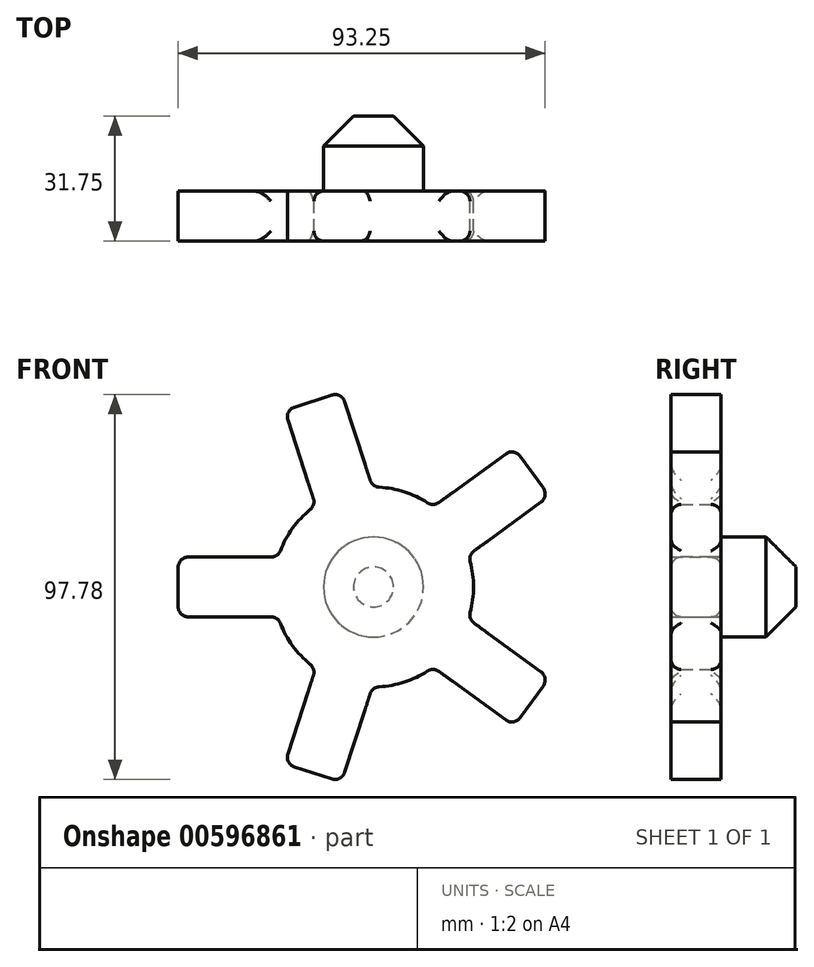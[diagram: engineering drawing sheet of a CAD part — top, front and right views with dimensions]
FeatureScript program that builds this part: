
annotation { "Feature Type Name" : "Feature", "Feature Type Description" : "" }
export const myFeature = defineFeature(function(context is Context, id is Id, definition is map)
    precondition{}
    {
        {
            var Q0;
            Q0=qCreatedBy(makeId("Front.planeOp"),FACE);
            var sketch = newSketch(context, id + "F0", { "sketchPlane" : qUnion([Q0])});
            skCircle(sketch, "E0", {"center": v(0, 0) * mm, "radius": 25.4 * mm});
            skLineSegment(sketch, "E1", {"start": v(-25.4, 0) * mm, "end": v(0, 0) * mm});
            skLineSegment(sketch, "E2.bottom", {"start": v(24.24, 7.59) * mm, "end": v(-49.64, 7.59) * mm});
            skLineSegment(sketch, "E2.top", {"start": v(24.24, -7.59) * mm, "end": v(-49.64, -7.59) * mm});
            skLineSegment(sketch, "E2.left", {"start": v(24.24, 7.59) * mm, "end": v(24.24, -7.59) * mm});
            skLineSegment(sketch, "E2.right", {"start": v(-49.64, 7.59) * mm, "end": v(-49.64, -7.59) * mm});
            skPoint(sketch, "E2.middle", {"position": v(-12.7, 0) * mm});
            skLineSegment(sketch, "E3.1.0", {"start": v(-22.56, -44.87) * mm, "end": v(-8.12, -49.56) * mm});
            skLineSegment(sketch, "E3.1.1", {"start": v(0.28, 25.4) * mm, "end": v(-22.56, -44.87) * mm});
            skLineSegment(sketch, "E3.1.2", {"start": v(14.7, 20.7) * mm, "end": v(-8.12, -49.56) * mm});
            skLineSegment(sketch, "E3.1.3", {"start": v(0.28, 25.4) * mm, "end": v(14.7, 20.7) * mm});
            skLineSegment(sketch, "E3.2.0", {"start": v(35.7, -35.32) * mm, "end": v(44.62, -23.04) * mm});
            skLineSegment(sketch, "E3.2.1", {"start": v(-24.07, 8.11) * mm, "end": v(35.7, -35.32) * mm});
            skLineSegment(sketch, "E3.2.2", {"start": v(-15.15, 20.39) * mm, "end": v(44.62, -23.04) * mm});
            skLineSegment(sketch, "E3.2.3", {"start": v(-24.07, 8.11) * mm, "end": v(-15.15, 20.39) * mm});
            skLineSegment(sketch, "E3.3.0", {"start": v(44.62, 23.04) * mm, "end": v(35.7, 35.32) * mm});
            skLineSegment(sketch, "E3.3.1", {"start": v(-15.15, -20.39) * mm, "end": v(44.62, 23.04) * mm});
            skLineSegment(sketch, "E3.3.2", {"start": v(-24.07, -8.11) * mm, "end": v(35.7, 35.32) * mm});
            skLineSegment(sketch, "E3.3.3", {"start": v(-15.15, -20.39) * mm, "end": v(-24.07, -8.11) * mm});
            skLineSegment(sketch, "E3.4.0", {"start": v(-8.12, 49.56) * mm, "end": v(-22.56, 44.87) * mm});
            skLineSegment(sketch, "E3.4.1", {"start": v(14.7, -20.7) * mm, "end": v(-8.12, 49.56) * mm});
            skLineSegment(sketch, "E3.4.2", {"start": v(0.28, -25.4) * mm, "end": v(-22.56, 44.87) * mm});
            skLineSegment(sketch, "E3.4.3", {"start": v(14.7, -20.7) * mm, "end": v(0.28, -25.4) * mm});
            skSolve(sketch);
        }
        {
            var Q0;
            Q0 = qSketchRegion(id + "F0", true);
            var Q1;
            {var subQ5=sQuery(id+"F0.wireOp",EDGE,"E3.2.2");var subQ6=sQuery(id+"F0.wireOp",EDGE,"E2.bottom");var subQ7=makeQuery(id+"F0.imprint","INTERSECT",VERTEX,{"derivedFrom":[subQ6,subQ5]});Q1=makeQuery(id+"F0.imprint","IMPRINT",FACE,{"disambiguationData":[TD([[makeQuery(id+"F0.imprint","IMPRINT",EDGE,{"disambiguationData":[TD([[subQ7,-1.0]])],"derivedFrom":subQ6}),1.0]])]});}
            var Q2;
            {var subQ0=sQuery(id+"F0.wireOp",EDGE,"E3.4.1");var subQ1=sQuery(id+"F0.wireOp",EDGE,"E3.1.1");var subQ2=makeQuery(id+"F0.imprint","INTERSECT",VERTEX,{"derivedFrom":[subQ1,subQ0]});Q2=makeQuery(id+"F0.imprint","IMPRINT",FACE,{"disambiguationData":[TD([[makeQuery(id+"F0.imprint","IMPRINT",EDGE,{"disambiguationData":[TD([[subQ2,-1.0]])],"derivedFrom":subQ1}),1.0]])]});}
            var Q3;
            {var subQ0=sQuery(id+"F0.wireOp",EDGE,"E3.1.2");var subQ1=sQuery(id+"F0.wireOp",EDGE,"E2.bottom");var subQ2=makeQuery(id+"F0.imprint","INTERSECT",VERTEX,{"derivedFrom":[subQ1,subQ0]});Q3=makeQuery(id+"F0.imprint","IMPRINT",FACE,{"disambiguationData":[TD([[makeQuery(id+"F0.imprint","IMPRINT",EDGE,{"disambiguationData":[TD([[subQ2,-1.0]])],"derivedFrom":subQ1}),-1.0]])]});}
            var Q4;
            {var subQ0=sQuery(id+"F0.wireOp",EDGE,"E3.3.1");var subQ1=sQuery(id+"F0.wireOp",EDGE,"E2.bottom");var subQ2=makeQuery(id+"F0.imprint","INTERSECT",VERTEX,{"derivedFrom":[subQ1,subQ0]});Q4=makeQuery(id+"F0.imprint","IMPRINT",FACE,{"disambiguationData":[TD([[makeQuery(id+"F0.imprint","IMPRINT",EDGE,{"disambiguationData":[TD([[subQ2,-1.0]])],"derivedFrom":subQ1}),1.0]])]});}
            var Q5;
            {var subQ0=sQuery(id+"F0.wireOp",EDGE,"E3.2.2");var subQ1=sQuery(id+"F0.wireOp",EDGE,"E2.top");var subQ2=makeQuery(id+"F0.imprint","INTERSECT",VERTEX,{"derivedFrom":[subQ1,subQ0]});Q5=makeQuery(id+"F0.imprint","IMPRINT",FACE,{"disambiguationData":[TD([[makeQuery(id+"F0.imprint","IMPRINT",EDGE,{"disambiguationData":[TD([[subQ2,-1.0]])],"derivedFrom":subQ1}),-1.0]])]});}
            var Q6;
            {var subQ0=sQuery(id+"F0.wireOp",EDGE,"E3.4.2");var subQ1=sQuery(id+"F0.wireOp",EDGE,"E2.top");var subQ2=makeQuery(id+"F0.imprint","INTERSECT",VERTEX,{"derivedFrom":[subQ1,subQ0]});Q6=makeQuery(id+"F0.imprint","IMPRINT",FACE,{"disambiguationData":[TD([[makeQuery(id+"F0.imprint","IMPRINT",EDGE,{"disambiguationData":[TD([[subQ2,-1.0]])],"derivedFrom":subQ1}),1.0]])]});}
            var Q7;
            {var subQ0=sQuery(id+"F0.wireOp",EDGE,"E3.4.1");var subQ1=sQuery(id+"F0.wireOp",EDGE,"E2.top");var subQ2=makeQuery(id+"F0.imprint","INTERSECT",VERTEX,{"derivedFrom":[subQ1,subQ0]});Q7=makeQuery(id+"F0.imprint","IMPRINT",FACE,{"disambiguationData":[TD([[makeQuery(id+"F0.imprint","IMPRINT",EDGE,{"disambiguationData":[TD([[subQ2,-1.0]])],"derivedFrom":subQ1}),1.0]])]});}
            var Q8;
            {var subQ0=sQuery(id+"F0.wireOp",EDGE,"E3.1.2");var subQ1=sQuery(id+"F0.wireOp",EDGE,"E2.top");var subQ2=makeQuery(id+"F0.imprint","INTERSECT",VERTEX,{"derivedFrom":[subQ1,subQ0]});Q8=makeQuery(id+"F0.imprint","IMPRINT",FACE,{"disambiguationData":[TD([[makeQuery(id+"F0.imprint","IMPRINT",EDGE,{"disambiguationData":[TD([[subQ2,-1.0]])],"derivedFrom":subQ1}),1.0]])]});}
            var Q9;
            {var subQ0=sQuery(id+"F0.wireOp",EDGE,"E3.2.1");var subQ1=sQuery(id+"F0.wireOp",EDGE,"E2.top");var subQ2=makeQuery(id+"F0.imprint","INTERSECT",VERTEX,{"derivedFrom":[subQ1,subQ0]});Q9=makeQuery(id+"F0.imprint","IMPRINT",FACE,{"disambiguationData":[TD([[makeQuery(id+"F0.imprint","IMPRINT",EDGE,{"disambiguationData":[TD([[subQ2,-1.0]])],"derivedFrom":subQ1}),1.0]])]});}
            var Q10;
            {var subQ0=sQuery(id+"F0.wireOp",EDGE,"E3.1.1");var subQ3=sQuery(id+"F0.wireOp",EDGE,"E3.2.1");var subQ5=makeQuery(id+"F0.imprint","INTERSECT",VERTEX,{"derivedFrom":[subQ0,subQ3]});Q10=makeQuery(id+"F0.imprint","IMPRINT",FACE,{"disambiguationData":[TD([[makeQuery(id+"F0.imprint","IMPRINT",EDGE,{"disambiguationData":[TD([[subQ5,1.0]])],"derivedFrom":subQ0}),-1.0]])]});}
            var Q11;
            {var subQ0=sQuery(id+"F0.wireOp",EDGE,"E3.4.2");var subQ1=sQuery(id+"F0.wireOp",EDGE,"E2.bottom");var subQ2=makeQuery(id+"F0.imprint","INTERSECT",VERTEX,{"derivedFrom":[subQ1,subQ0]});Q11=makeQuery(id+"F0.imprint","IMPRINT",FACE,{"disambiguationData":[TD([[makeQuery(id+"F0.imprint","IMPRINT",EDGE,{"disambiguationData":[TD([[subQ2,-1.0]])],"derivedFrom":subQ1}),1.0]])]});}
            var Q12;
            {var subQ0=sQuery(id+"F0.wireOp",EDGE,"E3.1.1");var subQ1=sQuery(id+"F0.wireOp",EDGE,"E2.bottom");var subQ2=makeQuery(id+"F0.imprint","INTERSECT",VERTEX,{"derivedFrom":[subQ1,subQ0]});Q12=makeQuery(id+"F0.imprint","IMPRINT",FACE,{"disambiguationData":[TD([[makeQuery(id+"F0.imprint","IMPRINT",EDGE,{"disambiguationData":[TD([[subQ2,-1.0]])],"derivedFrom":subQ1}),-1.0]])]});}
            var Q13;
            {var subQ0=sQuery(id+"F0.wireOp",EDGE,"E3.2.1");var subQ1=sQuery(id+"F0.wireOp",EDGE,"E3.1.2");var subQ2=makeQuery(id+"F0.imprint","INTERSECT",VERTEX,{"derivedFrom":[subQ1,subQ0]});Q13=makeQuery(id+"F0.imprint","IMPRINT",FACE,{"disambiguationData":[TD([[makeQuery(id+"F0.imprint","IMPRINT",EDGE,{"disambiguationData":[TD([[subQ2,-1.0]])],"derivedFrom":subQ1}),-1.0]])]});}
            var Q14;
            {var subQ0=sQuery(id+"F0.wireOp",EDGE,"E3.1.1");var subQ1=sQuery(id+"F0.wireOp",EDGE,"E2.top");var subQ2=makeQuery(id+"F0.imprint","INTERSECT",VERTEX,{"derivedFrom":[subQ1,subQ0]});Q14=makeQuery(id+"F0.imprint","IMPRINT",FACE,{"disambiguationData":[TD([[makeQuery(id+"F0.imprint","IMPRINT",EDGE,{"disambiguationData":[TD([[subQ2,-1.0]])],"derivedFrom":subQ1}),-1.0]])]});}
            var Q15;
            {var subQ0=sQuery(id+"F0.wireOp",EDGE,"E3.4.2");var subQ1=sQuery(id+"F0.wireOp",EDGE,"E2.top");var subQ2=makeQuery(id+"F0.imprint","INTERSECT",VERTEX,{"derivedFrom":[subQ1,subQ0]});Q15=makeQuery(id+"F0.imprint","IMPRINT",FACE,{"disambiguationData":[TD([[makeQuery(id+"F0.imprint","IMPRINT",EDGE,{"disambiguationData":[TD([[subQ2,-1.0]])],"derivedFrom":subQ1}),-1.0]])]});}
            var Q16;
            {var subQ0=sQuery(id+"F0.wireOp",EDGE,"E3.2.1");var subQ1=sQuery(id+"F0.wireOp",EDGE,"E3.1.1");var subQ2=makeQuery(id+"F0.imprint","INTERSECT",VERTEX,{"derivedFrom":[subQ1,subQ0]});Q16=makeQuery(id+"F0.imprint","IMPRINT",FACE,{"disambiguationData":[TD([[makeQuery(id+"F0.imprint","IMPRINT",EDGE,{"disambiguationData":[TD([[subQ2,-1.0]])],"derivedFrom":subQ0}),1.0]])]});}
            var Q17;
            {var subQ0=sQuery(id+"F0.wireOp",EDGE,"E3.4.2");var subQ3=sQuery(id+"F0.wireOp",EDGE,"E3.3.2");var subQ5=makeQuery(id+"F0.imprint","INTERSECT",VERTEX,{"derivedFrom":[subQ3,subQ0]});Q17=makeQuery(id+"F0.imprint","IMPRINT",FACE,{"disambiguationData":[TD([[makeQuery(id+"F0.imprint","IMPRINT",EDGE,{"disambiguationData":[TD([[subQ5,1.0]])],"derivedFrom":subQ3}),-1.0]])]});}
            var Q18;
            {var subQ0=sQuery(id+"F0.wireOp",EDGE,"E3.1.1");var subQ1=sQuery(id+"F0.wireOp",EDGE,"E2.bottom");var subQ2=makeQuery(id+"F0.imprint","INTERSECT",VERTEX,{"derivedFrom":[subQ1,subQ0]});Q18=makeQuery(id+"F0.imprint","IMPRINT",FACE,{"disambiguationData":[TD([[makeQuery(id+"F0.imprint","IMPRINT",EDGE,{"disambiguationData":[TD([[subQ2,-1.0]])],"derivedFrom":subQ1}),1.0]])]});}
            var Q19;
            {var subQ0=sQuery(id+"F0.wireOp",EDGE,"E3.3.2");var subQ1=sQuery(id+"F0.wireOp",EDGE,"E2.bottom");var subQ2=makeQuery(id+"F0.imprint","INTERSECT",VERTEX,{"derivedFrom":[subQ1,subQ0]});Q19=makeQuery(id+"F0.imprint","IMPRINT",FACE,{"disambiguationData":[TD([[makeQuery(id+"F0.imprint","IMPRINT",EDGE,{"disambiguationData":[TD([[subQ2,-1.0]])],"derivedFrom":subQ1}),-1.0]])]});}
            var Q20;
            {var subQ0=sQuery(id+"F0.wireOp",EDGE,"E3.4.1");var subQ1=sQuery(id+"F0.wireOp",EDGE,"E2.bottom");var subQ2=makeQuery(id+"F0.imprint","INTERSECT",VERTEX,{"derivedFrom":[subQ1,subQ0]});Q20=makeQuery(id+"F0.imprint","IMPRINT",FACE,{"disambiguationData":[TD([[makeQuery(id+"F0.imprint","IMPRINT",EDGE,{"disambiguationData":[TD([[subQ2,-1.0]])],"derivedFrom":subQ1}),-1.0]])]});}
            var Q21;
            {var subQ0=sQuery(id+"F0.wireOp",EDGE,"E3.4.1");var subQ1=sQuery(id+"F0.wireOp",EDGE,"E2.bottom");var subQ2=makeQuery(id+"F0.imprint","INTERSECT",VERTEX,{"derivedFrom":[subQ1,subQ0]});Q21=makeQuery(id+"F0.imprint","IMPRINT",FACE,{"disambiguationData":[TD([[makeQuery(id+"F0.imprint","IMPRINT",EDGE,{"disambiguationData":[TD([[subQ2,-1.0]])],"derivedFrom":subQ1}),1.0]])]});}
            var Q22;
            {var subQ0=sQuery(id+"F0.wireOp",EDGE,"E3.2.2");var subQ1=sQuery(id+"F0.wireOp",EDGE,"E3.1.2");var subQ2=makeQuery(id+"F0.imprint","INTERSECT",VERTEX,{"derivedFrom":[subQ1,subQ0]});Q22=makeQuery(id+"F0.imprint","IMPRINT",FACE,{"disambiguationData":[TD([[makeQuery(id+"F0.imprint","IMPRINT",EDGE,{"disambiguationData":[TD([[subQ2,-1.0]])],"derivedFrom":subQ1}),1.0]])]});}
            var Q23;
            {var subQ0=sQuery(id+"F0.wireOp",EDGE,"E3.2.2");var subQ1=sQuery(id+"F0.wireOp",EDGE,"E3.1.2");var subQ2=makeQuery(id+"F0.imprint","INTERSECT",VERTEX,{"derivedFrom":[subQ1,subQ0]});Q23=makeQuery(id+"F0.imprint","IMPRINT",FACE,{"disambiguationData":[TD([[makeQuery(id+"F0.imprint","IMPRINT",EDGE,{"disambiguationData":[TD([[subQ2,-1.0]])],"derivedFrom":subQ1}),-1.0]])]});}
            var Q24;
            {var subQ0=sQuery(id+"F0.wireOp",EDGE,"E3.4.1");var subQ1=sQuery(id+"F0.wireOp",EDGE,"E3.1.2");var subQ2=makeQuery(id+"F0.imprint","INTERSECT",VERTEX,{"derivedFrom":[subQ1,subQ0]});Q24=makeQuery(id+"F0.imprint","IMPRINT",FACE,{"disambiguationData":[TD([[makeQuery(id+"F0.imprint","IMPRINT",EDGE,{"disambiguationData":[TD([[subQ2,-1.0]])],"derivedFrom":subQ1}),1.0]])]});}
            var Q25;
            {var subQ0=sQuery(id+"F0.wireOp",EDGE,"E3.3.1");var subQ1=sQuery(id+"F0.wireOp",EDGE,"E2.top");var subQ2=makeQuery(id+"F0.imprint","INTERSECT",VERTEX,{"derivedFrom":[subQ1,subQ0]});Q25=makeQuery(id+"F0.imprint","IMPRINT",FACE,{"disambiguationData":[TD([[makeQuery(id+"F0.imprint","IMPRINT",EDGE,{"disambiguationData":[TD([[subQ2,-1.0]])],"derivedFrom":subQ1}),1.0]])]});}
            var Q26;
            {var subQ0=sQuery(id+"F0.wireOp",EDGE,"E3.2.1");var subQ1=sQuery(id+"F0.wireOp",EDGE,"E2.top");var subQ2=makeQuery(id+"F0.imprint","INTERSECT",VERTEX,{"derivedFrom":[subQ1,subQ0]});Q26=makeQuery(id+"F0.imprint","IMPRINT",FACE,{"disambiguationData":[TD([[makeQuery(id+"F0.imprint","IMPRINT",EDGE,{"disambiguationData":[TD([[subQ2,-1.0]])],"derivedFrom":subQ1}),-1.0]])]});}
            var Q27;
            {var subQ0=sQuery(id+"F0.wireOp",EDGE,"E3.3.2");var subQ1=sQuery(id+"F0.wireOp",EDGE,"E3.1.1");var subQ2=makeQuery(id+"F0.imprint","INTERSECT",VERTEX,{"derivedFrom":[subQ1,subQ0]});Q27=makeQuery(id+"F0.imprint","IMPRINT",FACE,{"disambiguationData":[TD([[makeQuery(id+"F0.imprint","IMPRINT",EDGE,{"disambiguationData":[TD([[subQ2,1.0]])],"derivedFrom":subQ0}),-1.0]])]});}
            var Q28;
            {var subQ0=sQuery(id+"F0.wireOp",EDGE,"E3.3.2");var subQ1=sQuery(id+"F0.wireOp",EDGE,"E2.bottom");var subQ2=makeQuery(id+"F0.imprint","INTERSECT",VERTEX,{"derivedFrom":[subQ1,subQ0]});Q28=makeQuery(id+"F0.imprint","IMPRINT",FACE,{"disambiguationData":[TD([[makeQuery(id+"F0.imprint","IMPRINT",EDGE,{"disambiguationData":[TD([[subQ2,-1.0]])],"derivedFrom":subQ1}),1.0]])]});}
            var Q29;
            {var subQ0=sQuery(id+"F0.wireOp",EDGE,"E3.2.2");var subQ1=sQuery(id+"F0.wireOp",EDGE,"E2.bottom");var subQ2=makeQuery(id+"F0.imprint","INTERSECT",VERTEX,{"derivedFrom":[subQ1,subQ0]});Q29=makeQuery(id+"F0.imprint","IMPRINT",FACE,{"disambiguationData":[TD([[makeQuery(id+"F0.imprint","IMPRINT",EDGE,{"disambiguationData":[TD([[subQ2,-1.0]])],"derivedFrom":subQ1}),-1.0]])]});}
            var Q30;
            {var subQ0=sQuery(id+"F0.wireOp",EDGE,"E3.1.2");var subQ1=sQuery(id+"F0.wireOp",EDGE,"E2.bottom");var subQ2=makeQuery(id+"F0.imprint","INTERSECT",VERTEX,{"derivedFrom":[subQ1,subQ0]});Q30=makeQuery(id+"F0.imprint","IMPRINT",FACE,{"disambiguationData":[TD([[makeQuery(id+"F0.imprint","IMPRINT",EDGE,{"disambiguationData":[TD([[subQ2,-1.0]])],"derivedFrom":subQ1}),1.0]])]});}
            var Q31;
            {var subQ0=sQuery(id+"F0.wireOp",EDGE,"E3.4.1");var subQ1=sQuery(id+"F0.wireOp",EDGE,"E2.top");var subQ2=makeQuery(id+"F0.imprint","INTERSECT",VERTEX,{"derivedFrom":[subQ1,subQ0]});Q31=makeQuery(id+"F0.imprint","IMPRINT",FACE,{"disambiguationData":[TD([[makeQuery(id+"F0.imprint","IMPRINT",EDGE,{"disambiguationData":[TD([[subQ2,-1.0]])],"derivedFrom":subQ1}),-1.0]])]});}
            var Q32;
            {var subQ0=sQuery(id+"F0.wireOp",EDGE,"E3.1.2");var subQ1=sQuery(id+"F0.wireOp",EDGE,"E2.top");var subQ2=makeQuery(id+"F0.imprint","INTERSECT",VERTEX,{"derivedFrom":[subQ1,subQ0]});Q32=makeQuery(id+"F0.imprint","IMPRINT",FACE,{"disambiguationData":[TD([[makeQuery(id+"F0.imprint","IMPRINT",EDGE,{"disambiguationData":[TD([[subQ2,-1.0]])],"derivedFrom":subQ1}),-1.0]])]});}
            extrude(context, id + "F1", {"entities" : qUnion([Q0, Q1, Q2, Q3, Q4, Q5, Q6, Q7, Q8, Q9, Q10, Q11, Q12, Q13, Q14, Q15, Q16, Q17, Q18, Q19, Q20, Q21, Q22, Q23, Q24, Q25, Q26, Q27, Q28, Q29, Q30, Q31, Q32]), "depth" : 12.7 * mm, "offsetDistance" : 25.4 * mm});
        }
        {
            var Q0;
            Q0=makeQuery(id+"F1.opExtrude","SWEPT_EDGE",EDGE,{"disambiguationData":[OSD([sQuery(id+"F0.wireOp",EDGE,"E3.3.0"),sQuery(id+"F0.wireOp",EDGE,"E3.3.1")])]});
            var Q1;
            Q1=makeQuery(id+"F1.opExtrude","SWEPT_EDGE",EDGE,{"disambiguationData":[OSD([sQuery(id+"F0.wireOp",EDGE,"E3.2.0"),sQuery(id+"F0.wireOp",EDGE,"E3.2.2")])]});
            var Q2;
            Q2=makeQuery(id+"F1.opExtrude","SWEPT_EDGE",EDGE,{"disambiguationData":[OSD([sQuery(id+"F0.wireOp",EDGE,"E3.2.0"),sQuery(id+"F0.wireOp",EDGE,"E3.2.1")])]});
            var Q3;
            Q3=makeQuery(id+"F1.opExtrude","SWEPT_EDGE",EDGE,{"disambiguationData":[OSD([sQuery(id+"F0.wireOp",EDGE,"E3.1.0"),sQuery(id+"F0.wireOp",EDGE,"E3.1.2")])]});
            var Q4;
            Q4=makeQuery(id+"F1.opExtrude","SWEPT_EDGE",EDGE,{"disambiguationData":[OSD([sQuery(id+"F0.wireOp",EDGE,"E3.1.0"),sQuery(id+"F0.wireOp",EDGE,"E3.1.1")])]});
            var Q5;
            Q5=makeQuery(id+"F1.opExtrude","SWEPT_EDGE",EDGE,{"disambiguationData":[OSD([sQuery(id+"F0.wireOp",EDGE,"E2.top"),sQuery(id+"F0.wireOp",EDGE,"E2.right")])]});
            var Q6;
            Q6=makeQuery(id+"F1.opExtrude","SWEPT_EDGE",EDGE,{"disambiguationData":[OSD([sQuery(id+"F0.wireOp",EDGE,"E2.bottom"),sQuery(id+"F0.wireOp",EDGE,"E2.right")])]});
            var Q7;
            Q7=makeQuery(id+"F1.opExtrude","SWEPT_EDGE",EDGE,{"disambiguationData":[OSD([sQuery(id+"F0.wireOp",EDGE,"E3.3.0"),sQuery(id+"F0.wireOp",EDGE,"E3.3.2")])]});
            var Q8;
            Q8=makeQuery(id+"F1.opExtrude","SWEPT_EDGE",EDGE,{"disambiguationData":[OSD([sQuery(id+"F0.wireOp",EDGE,"E3.4.0"),sQuery(id+"F0.wireOp",EDGE,"E3.4.1")])]});
            var Q9;
            Q9=makeQuery(id+"F1.opExtrude","SWEPT_EDGE",EDGE,{"disambiguationData":[OSD([sQuery(id+"F0.wireOp",EDGE,"E3.4.0"),sQuery(id+"F0.wireOp",EDGE,"E3.4.2")])]});
            fillet(context, id + "F2", {"entities" : qUnion([Q0, Q1, Q2, Q3, Q4, Q5, Q6, Q7, Q8, Q9]), "radius" : 2.54 * mm, "tangentPropagation" : true, "allowEdgeOverflow" : false});
        }
        {
            var Q0;
            {var subQ0=sQuery(id+"F0.wireOp",EDGE,"E3.4.3");var subQ1=sQuery(id+"F0.wireOp",EDGE,"E0");var subQ2=makeQuery(id+"F0.imprint","INTERSECT",VERTEX,{"derivedFrom":[subQ1,sQuery(id+"F0.wireOp",EDGE,"E3.4.1"),subQ0]});Q0=makeQuery(id+"F1.opExtrude","CAP_EDGE",EDGE,{"disambiguationData":[OSD([subQ1]),TDD([makeQuery(id+"F0.imprint","IMPRINT",EDGE,{"disambiguationData":[TD([[makeQuery(id+"F0.imprint","INTERSECT",VERTEX,{"derivedFrom":[subQ1,sQuery(id+"F0.wireOp",EDGE,"E3.1.2")]}),-1.0]])],"derivedFrom":subQ1}),makeQuery(id+"F0.imprint","IMPRINT",EDGE,{"disambiguationData":[TD([[subQ2,1.0]])],"derivedFrom":subQ1}),makeQuery(id+"F0.imprint","IMPRINT",EDGE,{"disambiguationData":[TD([[makeQuery(id+"F0.imprint","INTERSECT",VERTEX,{"derivedFrom":[subQ1,sQuery(id+"F0.wireOp",EDGE,"E3.2.1")]}),1.0]])],"derivedFrom":subQ1})])],"isStart":true});}
            var Q1;
            {var subQ0=sQuery(id+"F0.wireOp",EDGE,"E3.4.3");var subQ1=sQuery(id+"F0.wireOp",EDGE,"E0");var subQ2=makeQuery(id+"F0.imprint","INTERSECT",VERTEX,{"derivedFrom":[subQ1,sQuery(id+"F0.wireOp",EDGE,"E3.4.1"),subQ0]});Q1=makeQuery(id+"F1.opExtrude","CAP_EDGE",EDGE,{"disambiguationData":[OSD([subQ1]),TDD([makeQuery(id+"F0.imprint","IMPRINT",EDGE,{"disambiguationData":[TD([[makeQuery(id+"F0.imprint","INTERSECT",VERTEX,{"derivedFrom":[subQ1,sQuery(id+"F0.wireOp",EDGE,"E3.1.2")]}),-1.0]])],"derivedFrom":subQ1}),makeQuery(id+"F0.imprint","IMPRINT",EDGE,{"disambiguationData":[TD([[subQ2,1.0]])],"derivedFrom":subQ1}),makeQuery(id+"F0.imprint","IMPRINT",EDGE,{"disambiguationData":[TD([[makeQuery(id+"F0.imprint","INTERSECT",VERTEX,{"derivedFrom":[subQ1,sQuery(id+"F0.wireOp",EDGE,"E3.2.1")]}),1.0]])],"derivedFrom":subQ1})])],"isStart":false});}
            var Q2;
            {var subQ0=sQuery(id+"F0.wireOp",EDGE,"E2.left");var subQ1=sQuery(id+"F0.wireOp",EDGE,"E0");var subQ2=makeQuery(id+"F0.imprint","INTERSECT",VERTEX,{"derivedFrom":[subQ1,sQuery(id+"F0.wireOp",EDGE,"E2.bottom"),subQ0]});Q2=makeQuery(id+"F1.opExtrude","CAP_EDGE",EDGE,{"disambiguationData":[OSD([subQ1]),TDD([makeQuery(id+"F0.imprint","IMPRINT",EDGE,{"disambiguationData":[TD([[makeQuery(id+"F0.imprint","INTERSECT",VERTEX,{"derivedFrom":[subQ1,sQuery(id+"F0.wireOp",EDGE,"E3.3.1")]}),1.0]])],"derivedFrom":subQ1}),makeQuery(id+"F0.imprint","IMPRINT",EDGE,{"disambiguationData":[TD([[makeQuery(id+"F0.imprint","INTERSECT",VERTEX,{"derivedFrom":[subQ1,sQuery(id+"F0.wireOp",EDGE,"E3.2.2")]}),-1.0]])],"derivedFrom":subQ1}),makeQuery(id+"F0.imprint","IMPRINT",EDGE,{"disambiguationData":[TD([[subQ2,1.0]])],"derivedFrom":subQ1})])],"isStart":false});}
            var Q3;
            {var subQ0=sQuery(id+"F0.wireOp",EDGE,"E2.left");var subQ1=sQuery(id+"F0.wireOp",EDGE,"E0");var subQ2=makeQuery(id+"F0.imprint","INTERSECT",VERTEX,{"derivedFrom":[subQ1,sQuery(id+"F0.wireOp",EDGE,"E2.bottom"),subQ0]});Q3=makeQuery(id+"F1.opExtrude","CAP_EDGE",EDGE,{"disambiguationData":[OSD([subQ1]),TDD([makeQuery(id+"F0.imprint","IMPRINT",EDGE,{"disambiguationData":[TD([[makeQuery(id+"F0.imprint","INTERSECT",VERTEX,{"derivedFrom":[subQ1,sQuery(id+"F0.wireOp",EDGE,"E3.3.1")]}),1.0]])],"derivedFrom":subQ1}),makeQuery(id+"F0.imprint","IMPRINT",EDGE,{"disambiguationData":[TD([[makeQuery(id+"F0.imprint","INTERSECT",VERTEX,{"derivedFrom":[subQ1,sQuery(id+"F0.wireOp",EDGE,"E3.2.2")]}),-1.0]])],"derivedFrom":subQ1}),makeQuery(id+"F0.imprint","IMPRINT",EDGE,{"disambiguationData":[TD([[subQ2,1.0]])],"derivedFrom":subQ1})])],"isStart":true});}
            var Q4;
            {var subQ0=sQuery(id+"F0.wireOp",EDGE,"E3.1.3");var subQ1=sQuery(id+"F0.wireOp",EDGE,"E0");var subQ2=makeQuery(id+"F0.imprint","INTERSECT",VERTEX,{"derivedFrom":[subQ1,sQuery(id+"F0.wireOp",EDGE,"E3.1.1"),subQ0]});Q4=makeQuery(id+"F1.opExtrude","CAP_EDGE",EDGE,{"disambiguationData":[OSD([subQ1]),TDD([makeQuery(id+"F0.imprint","IMPRINT",EDGE,{"disambiguationData":[TD([[makeQuery(id+"F0.imprint","INTERSECT",VERTEX,{"derivedFrom":[subQ1,sQuery(id+"F0.wireOp",EDGE,"E3.3.2")]}),-1.0]])],"derivedFrom":subQ1}),makeQuery(id+"F0.imprint","IMPRINT",EDGE,{"disambiguationData":[TD([[subQ2,1.0]])],"derivedFrom":subQ1}),makeQuery(id+"F0.imprint","IMPRINT",EDGE,{"disambiguationData":[TD([[makeQuery(id+"F0.imprint","INTERSECT",VERTEX,{"derivedFrom":[subQ1,sQuery(id+"F0.wireOp",EDGE,"E3.4.1")]}),1.0]])],"derivedFrom":subQ1})])],"isStart":false});}
            var Q5;
            {var subQ0=sQuery(id+"F0.wireOp",EDGE,"E3.1.3");var subQ1=sQuery(id+"F0.wireOp",EDGE,"E0");var subQ2=makeQuery(id+"F0.imprint","INTERSECT",VERTEX,{"derivedFrom":[subQ1,sQuery(id+"F0.wireOp",EDGE,"E3.1.1"),subQ0]});Q5=makeQuery(id+"F1.opExtrude","CAP_EDGE",EDGE,{"disambiguationData":[OSD([subQ1]),TDD([makeQuery(id+"F0.imprint","IMPRINT",EDGE,{"disambiguationData":[TD([[makeQuery(id+"F0.imprint","INTERSECT",VERTEX,{"derivedFrom":[subQ1,sQuery(id+"F0.wireOp",EDGE,"E3.3.2")]}),-1.0]])],"derivedFrom":subQ1}),makeQuery(id+"F0.imprint","IMPRINT",EDGE,{"disambiguationData":[TD([[subQ2,1.0]])],"derivedFrom":subQ1}),makeQuery(id+"F0.imprint","IMPRINT",EDGE,{"disambiguationData":[TD([[makeQuery(id+"F0.imprint","INTERSECT",VERTEX,{"derivedFrom":[subQ1,sQuery(id+"F0.wireOp",EDGE,"E3.4.1")]}),1.0]])],"derivedFrom":subQ1})])],"isStart":true});}
            var Q6;
            {var subQ0=sQuery(id+"F0.wireOp",EDGE,"E3.2.3");var subQ1=sQuery(id+"F0.wireOp",EDGE,"E0");var subQ2=makeQuery(id+"F0.imprint","INTERSECT",VERTEX,{"derivedFrom":[subQ1,sQuery(id+"F0.wireOp",EDGE,"E3.2.1"),subQ0]});Q6=makeQuery(id+"F1.opExtrude","SWEPT_FACE",FACE,{"disambiguationData":[OSD([subQ1]),TDD([makeQuery(id+"F0.imprint","IMPRINT",EDGE,{"disambiguationData":[TD([[makeQuery(id+"F0.imprint","INTERSECT",VERTEX,{"derivedFrom":[subQ1,sQuery(id+"F0.wireOp",EDGE,"E3.4.2")]}),-1.0]])],"derivedFrom":subQ1}),makeQuery(id+"F0.imprint","IMPRINT",EDGE,{"disambiguationData":[TD([[subQ2,1.0]])],"derivedFrom":subQ1}),makeQuery(id+"F0.imprint","IMPRINT",EDGE,{"disambiguationData":[TD([[makeQuery(id+"F0.imprint","INTERSECT",VERTEX,{"derivedFrom":[subQ1,sQuery(id+"F0.wireOp",EDGE,"E2.bottom")]}),1.0]])],"derivedFrom":subQ1})])]});}
            var Q7;
            {var subQ0=sQuery(id+"F0.wireOp",EDGE,"E3.3.3");var subQ1=sQuery(id+"F0.wireOp",EDGE,"E0");var subQ2=makeQuery(id+"F0.imprint","INTERSECT",VERTEX,{"derivedFrom":[subQ1,sQuery(id+"F0.wireOp",EDGE,"E3.3.1"),subQ0]});Q7=makeQuery(id+"F1.opExtrude","SWEPT_FACE",FACE,{"disambiguationData":[OSD([subQ1]),TDD([makeQuery(id+"F0.imprint","IMPRINT",EDGE,{"disambiguationData":[TD([[makeQuery(id+"F0.imprint","INTERSECT",VERTEX,{"derivedFrom":[subQ1,sQuery(id+"F0.wireOp",EDGE,"E2.top")]}),-1.0]])],"derivedFrom":subQ1}),makeQuery(id+"F0.imprint","IMPRINT",EDGE,{"disambiguationData":[TD([[subQ2,1.0]])],"derivedFrom":subQ1}),makeQuery(id+"F0.imprint","IMPRINT",EDGE,{"disambiguationData":[TD([[makeQuery(id+"F0.imprint","INTERSECT",VERTEX,{"derivedFrom":[subQ1,sQuery(id+"F0.wireOp",EDGE,"E3.1.1")]}),1.0]])],"derivedFrom":subQ1})])]});}
            var Q8;
            {var subQ0=sQuery(id+"F0.wireOp",EDGE,"E3.4.3");var subQ1=sQuery(id+"F0.wireOp",EDGE,"E0");var subQ2=makeQuery(id+"F0.imprint","INTERSECT",VERTEX,{"derivedFrom":[subQ1,sQuery(id+"F0.wireOp",EDGE,"E3.4.1"),subQ0]});Q8=makeQuery(id+"F1.opExtrude","SWEPT_FACE",FACE,{"disambiguationData":[OSD([subQ1]),TDD([makeQuery(id+"F0.imprint","IMPRINT",EDGE,{"disambiguationData":[TD([[makeQuery(id+"F0.imprint","INTERSECT",VERTEX,{"derivedFrom":[subQ1,sQuery(id+"F0.wireOp",EDGE,"E3.1.2")]}),-1.0]])],"derivedFrom":subQ1}),makeQuery(id+"F0.imprint","IMPRINT",EDGE,{"disambiguationData":[TD([[subQ2,1.0]])],"derivedFrom":subQ1}),makeQuery(id+"F0.imprint","IMPRINT",EDGE,{"disambiguationData":[TD([[makeQuery(id+"F0.imprint","INTERSECT",VERTEX,{"derivedFrom":[subQ1,sQuery(id+"F0.wireOp",EDGE,"E3.2.1")]}),1.0]])],"derivedFrom":subQ1})])]});}
            var Q9;
            {var subQ0=sQuery(id+"F0.wireOp",EDGE,"E2.left");var subQ1=sQuery(id+"F0.wireOp",EDGE,"E0");var subQ2=makeQuery(id+"F0.imprint","INTERSECT",VERTEX,{"derivedFrom":[subQ1,sQuery(id+"F0.wireOp",EDGE,"E2.bottom"),subQ0]});Q9=makeQuery(id+"F1.opExtrude","SWEPT_FACE",FACE,{"disambiguationData":[OSD([subQ1]),TDD([makeQuery(id+"F0.imprint","IMPRINT",EDGE,{"disambiguationData":[TD([[makeQuery(id+"F0.imprint","INTERSECT",VERTEX,{"derivedFrom":[subQ1,sQuery(id+"F0.wireOp",EDGE,"E3.3.1")]}),1.0]])],"derivedFrom":subQ1}),makeQuery(id+"F0.imprint","IMPRINT",EDGE,{"disambiguationData":[TD([[makeQuery(id+"F0.imprint","INTERSECT",VERTEX,{"derivedFrom":[subQ1,sQuery(id+"F0.wireOp",EDGE,"E3.2.2")]}),-1.0]])],"derivedFrom":subQ1}),makeQuery(id+"F0.imprint","IMPRINT",EDGE,{"disambiguationData":[TD([[subQ2,1.0]])],"derivedFrom":subQ1})])]});}
            var Q10;
            {var subQ0=sQuery(id+"F0.wireOp",EDGE,"E3.1.3");var subQ1=sQuery(id+"F0.wireOp",EDGE,"E0");var subQ2=makeQuery(id+"F0.imprint","INTERSECT",VERTEX,{"derivedFrom":[subQ1,sQuery(id+"F0.wireOp",EDGE,"E3.1.1"),subQ0]});Q10=makeQuery(id+"F1.opExtrude","SWEPT_FACE",FACE,{"disambiguationData":[OSD([subQ1]),TDD([makeQuery(id+"F0.imprint","IMPRINT",EDGE,{"disambiguationData":[TD([[makeQuery(id+"F0.imprint","INTERSECT",VERTEX,{"derivedFrom":[subQ1,sQuery(id+"F0.wireOp",EDGE,"E3.3.2")]}),-1.0]])],"derivedFrom":subQ1}),makeQuery(id+"F0.imprint","IMPRINT",EDGE,{"disambiguationData":[TD([[subQ2,1.0]])],"derivedFrom":subQ1}),makeQuery(id+"F0.imprint","IMPRINT",EDGE,{"disambiguationData":[TD([[makeQuery(id+"F0.imprint","INTERSECT",VERTEX,{"derivedFrom":[subQ1,sQuery(id+"F0.wireOp",EDGE,"E3.4.1")]}),1.0]])],"derivedFrom":subQ1})])]});}
            fillet(context, id + "F3", {"entities" : qUnion([Q0, Q1, Q2, Q3, Q4, Q5, Q6, Q7, Q8, Q9, Q10]), "radius" : 2.54 * mm, "tangentPropagation" : true, "allowEdgeOverflow" : false});
        }
        {
            var Q0;
            Q0=makeQuery(id+"F1.opExtrude","CAP_FACE",FACE,{"disambiguationData":[OSD([sQuery(id+"F0.wireOp",EDGE,"E0"),sQuery(id+"F0.wireOp",EDGE,"E2.bottom"),sQuery(id+"F0.wireOp",EDGE,"E2.top"),sQuery(id+"F0.wireOp",EDGE,"E2.right"),sQuery(id+"F0.wireOp",EDGE,"E3.1.0"),sQuery(id+"F0.wireOp",EDGE,"E3.1.1"),sQuery(id+"F0.wireOp",EDGE,"E3.1.2"),sQuery(id+"F0.wireOp",EDGE,"E3.2.0"),sQuery(id+"F0.wireOp",EDGE,"E3.2.1"),sQuery(id+"F0.wireOp",EDGE,"E3.2.2"),sQuery(id+"F0.wireOp",EDGE,"E3.3.0"),sQuery(id+"F0.wireOp",EDGE,"E3.3.1"),sQuery(id+"F0.wireOp",EDGE,"E3.3.2"),sQuery(id+"F0.wireOp",EDGE,"E3.4.0"),sQuery(id+"F0.wireOp",EDGE,"E3.4.1"),sQuery(id+"F0.wireOp",EDGE,"E3.4.2")])],"isStart":true});
            var sketch = newSketch(context, id + "F4", { "sketchPlane" : qUnion([Q0])});
            skCircle(sketch, "E4", {"center": v(0, 0) * mm, "radius": 12.7 * mm});
            skSolve(sketch);
        }
        {
            var Q0;
            Q0 = qSketchRegion(id + "F4", true);
            extrude(context, id + "F5", {"entities" : qUnion([Q0]), "operationType" : NewBodyOperationType.ADD, "depth" : 19.05 * mm, "offsetDistance" : 25.4 * mm});
        }
        {
            var Q0;
            Q0=makeQuery(id+"F5.opExtrude","CAP_EDGE",EDGE,{"disambiguationData":[OSD([sQuery(id+"F4.wireOp",EDGE,"E4")])],"isStart":false});
            chamfer(context, id + "F6", {"entities" : qUnion([Q0]), "width" : 7.62 * mm, "tangentPropagation" : true});
        }
    });
